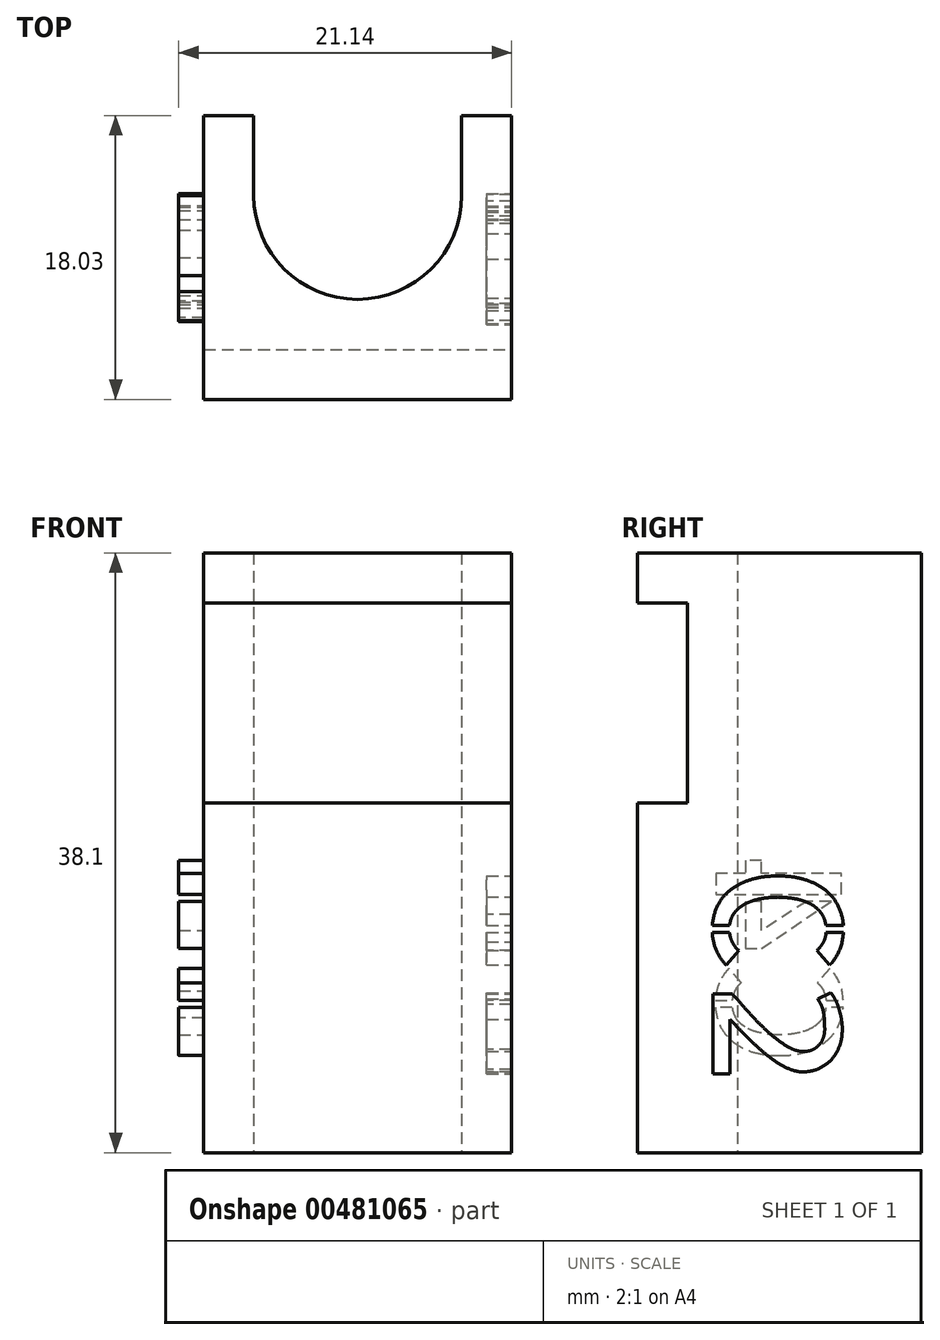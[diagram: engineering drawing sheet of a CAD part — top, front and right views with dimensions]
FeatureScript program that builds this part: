
annotation { "Feature Type Name" : "Feature", "Feature Type Description" : "" }
export const myFeature = defineFeature(function(context is Context, id is Id, definition is map)
    precondition{}
    {
        {
            var Q0;
            Q0=qCreatedBy(makeId("Top.planeOp"),FACE);
            var sketch = newSketch(context, id + "F0", { "sketchPlane" : qUnion([Q0])});
            skArc(sketch, "E0", {"start": v(-6.6, 0) * mm, "mid": v(0, -6.6) * mm, "end": v(6.6, 0) * mm});
            skLineSegment(sketch, "E1", {"start": v(-6.6, 0) * mm, "end": v(-6.6, 5.08) * mm});
            skLineSegment(sketch, "E2", {"start": v(6.6, 0) * mm, "end": v(6.6, 5.08) * mm});
            skLineSegment(sketch, "E3", {"start": v(-9.78, 5.08) * mm, "end": v(-9.77, -12.95) * mm});
            skLineSegment(sketch, "E4", {"start": v(-9.77, -12.95) * mm, "end": v(9.78, -12.95) * mm});
            skLineSegment(sketch, "E5", {"start": v(9.78, -12.95) * mm, "end": v(9.78, 5.08) * mm});
            skLineSegment(sketch, "E6", {"start": v(9.78, 5.08) * mm, "end": v(6.6, 5.08) * mm});
            skLineSegment(sketch, "E7", {"start": v(-6.6, 5.08) * mm, "end": v(-9.78, 5.08) * mm});
            skSolve(sketch);
        }
        {
            var Q0;
            Q0=makeQuery(id+"F0.imprint","IMPRINT",FACE,{"disambiguationData":[TD([[makeQuery(id+"F0.imprint","IMPRINT",EDGE,{"derivedFrom":sQuery(id+"F0.wireOp",EDGE,"E0")}),-1.0]])]});
            extrude(context, id + "F1", {"entities" : qUnion([Q0]), "depth" : 38.1 * mm});
        }
        {
            var Q0;
            Q0=makeQuery(id+"F1.opExtrude","SWEPT_FACE",FACE,{"disambiguationData":[OSD([sQuery(id+"F0.wireOp",EDGE,"E5")])]});
            var sketch = newSketch(context, id + "F2", { "sketchPlane" : qUnion([Q0])});
            skLineSegment(sketch, "E8.bottom", {"start": v(-12.95, 34.93) * mm, "end": v(-9.77, 34.93) * mm});
            skLineSegment(sketch, "E8.top", {"start": v(-12.95, 22.23) * mm, "end": v(-9.77, 22.23) * mm});
            skLineSegment(sketch, "E8.left", {"start": v(-12.95, 34.93) * mm, "end": v(-12.95, 22.23) * mm});
            skLineSegment(sketch, "E8.right", {"start": v(-9.77, 34.93) * mm, "end": v(-9.77, 22.23) * mm});
            skSolve(sketch);
        }
        {
            var Q0;
            Q0=makeQuery(id+"F2.imprint","IMPRINT",FACE,{"disambiguationData":[TD([[makeQuery(id+"F2.imprint","IMPRINT",EDGE,{"derivedFrom":sQuery(id+"F2.wireOp",EDGE,"E8.bottom")}),-1.0]])]});
            extrude(context, id + "F3", {"entities" : qUnion([Q0]), "operationType" : NewBodyOperationType.REMOVE, "endBound" : BoundingType.THROUGH_ALL, "oppositeDirection" : true, "depth" : 25.4 * mm});
        }
        {
            var Q0;
            Q0=makeQuery(id+"F1.opExtrude","SWEPT_FACE",FACE,{"disambiguationData":[OSD([sQuery(id+"F0.wireOp",EDGE,"E5")])]});
            var sketch = newSketch(context, id + "F4", { "sketchPlane" : qUnion([Q0])});
            skText(sketch, "E9", { "text": "C2", "fontName": "AllertaStencil-Regular.ttf"});
            const initialGuessF4  = {"E9": [-0.00815, 0.01845, 0, -1, 0.00815]};
            skSetInitialGuess(sketch, initialGuessF4);
            skSolve(sketch);
        }
        {
            var Q0;
            Q0 = qSketchRegion(id + "F4", true);
            extrude(context, id + "F5", {"entities" : qUnion([Q0]), "operationType" : NewBodyOperationType.REMOVE, "oppositeDirection" : true, "depth" : 1.59 * mm});
        }
        {
            var Q0;
            Q0=makeQuery(id+"F1.opExtrude","SWEPT_FACE",FACE,{"disambiguationData":[OSD([sQuery(id+"F0.wireOp",EDGE,"E3")])]});
            var sketch = newSketch(context, id + "F6", { "sketchPlane" : qUnion([Q0])});
            skText(sketch, "E10", { "text": "C4", "fontName": "AllertaStencil-Regular.ttf"});
            const initialGuessF6  = {"E10": [0.00796, 0.00531, 0, 1, 0.00796]};
            skSetInitialGuess(sketch, initialGuessF6);
            skSolve(sketch);
        }
        {
            var Q0;
            Q0 = qSketchRegion(id + "F6", true);
            extrude(context, id + "F7", {"entities" : qUnion([Q0]), "operationType" : NewBodyOperationType.ADD, "depth" : 1.59 * mm});
        }
    });
